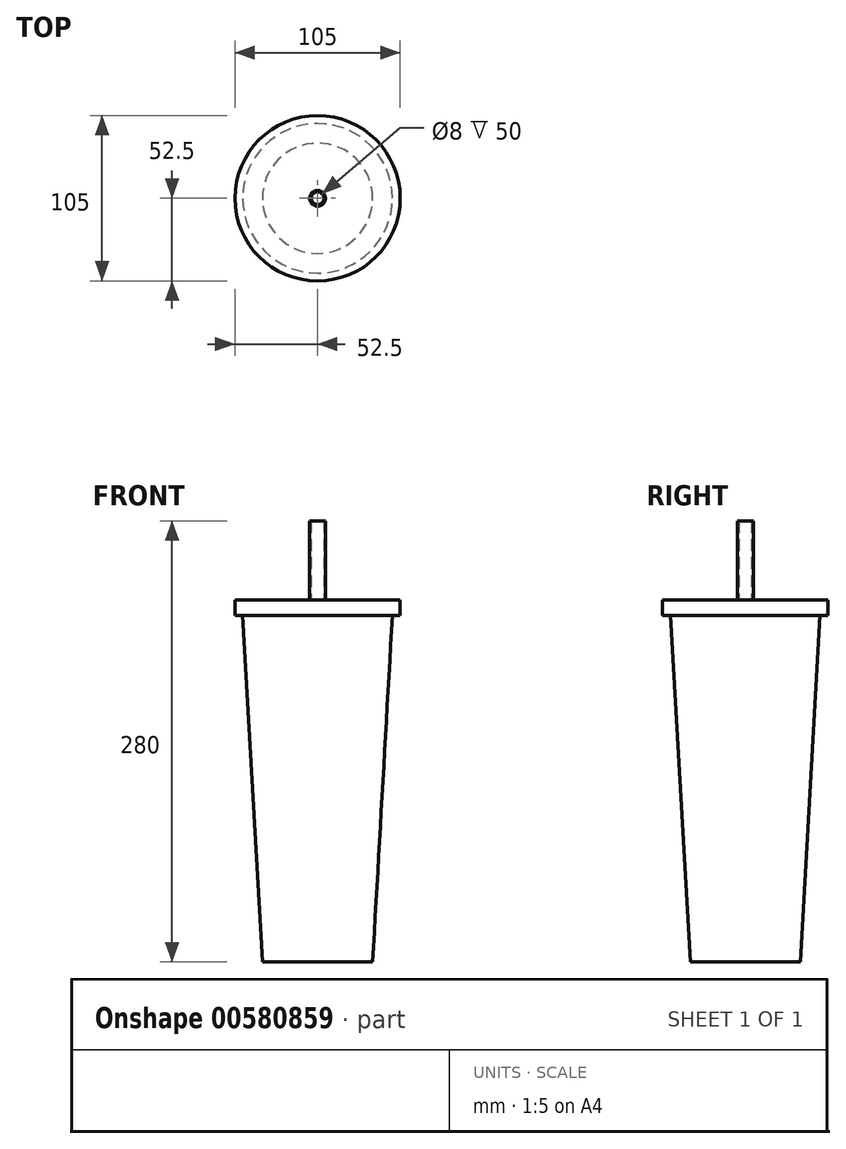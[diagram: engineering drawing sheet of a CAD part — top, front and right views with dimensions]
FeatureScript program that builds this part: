
annotation { "Feature Type Name" : "Feature", "Feature Type Description" : "" }
export const myFeature = defineFeature(function(context is Context, id is Id, definition is map)
    precondition{}
    {
        {
            var Q0;
            Q0=qCreatedBy(makeId("Top.planeOp"),FACE);
            var sketch = newSketch(context, id + "F0", { "sketchPlane" : qUnion([Q0])});
            skCircle(sketch, "E0", {"center": v(0, 0) * mm, "radius": 47.5 * mm});
            skSolve(sketch);
        }
        {
            var Q0;
            Q0=qCreatedBy(makeId("Top.planeOp"),FACE);
            cPlane(context, id + "F1", {"entities" : qUnion([Q0]), "cplaneType" : CPlaneType.OFFSET, "offset" : 220 * mm, "oppositeDirection" : true, "width" : 150 * mm, "height" : 150 * mm});
        }
        {
            var Q0;
            Q0=qCreatedBy(id+"F1.planeOp",FACE);
            var sketch = newSketch(context, id + "F2", { "sketchPlane" : qUnion([Q0])});
            skCircle(sketch, "E1", {"center": v(0, 0) * mm, "radius": 35 * mm});
            skSolve(sketch);
        }
        {
            var Q0;
            Q0=makeQuery(id+"F0.imprint","IMPRINT",FACE,{"disambiguationData":[TD([[makeQuery(id+"F0.imprint","IMPRINT",EDGE,{"derivedFrom":sQuery(id+"F0.wireOp",EDGE,"E0")}),1.0]])]});
            var Q1;
            Q1=makeQuery(id+"F2.imprint","IMPRINT",FACE,{"disambiguationData":[TD([[makeQuery(id+"F2.imprint","IMPRINT",EDGE,{"derivedFrom":sQuery(id+"F2.wireOp",EDGE,"E1")}),1.0]])]});
            loft(context, id + "F3", {"sheetProfilesArray" : [{ "sheetProfileEntities" : qUnion([Q0]) }, { "sheetProfileEntities" : qUnion([Q1]) }]});
        }
        {
            var Q0;
            Q0=makeQuery(id+"F3.opLoft","CAP_FACE",FACE,{"disambiguationData":[OSD([makeQuery(id+"F0.imprint","IMPRINT",FACE,{"disambiguationData":[TD([[makeQuery(id+"F0.imprint","IMPRINT",EDGE,{"derivedFrom":sQuery(id+"F0.wireOp",EDGE,"E0")}),1.0]])]})])],"isStart":true});
            var sketch = newSketch(context, id + "F4", { "sketchPlane" : qUnion([Q0])});
            skCircle(sketch, "E2", {"center": v(0, 0) * mm, "radius": 52.5 * mm});
            skSolve(sketch);
        }
        {
            var Q0;
            Q0=makeQuery(id+"F4.imprint","IMPRINT",FACE,{"disambiguationData":[TD([[makeQuery(id+"F4.imprint","IMPRINT",EDGE,{"derivedFrom":makeQuery(id+"F3.opLoft","MID_CAP_EDGE",EDGE,{"disambiguationData":[OSD([sQuery(id+"F0.wireOp",EDGE,"E0")])],"capPos":0.0})}),-1.0]])]});
            var Q1;
            Q1=makeQuery(id+"F4.imprint","IMPRINT",FACE,{"disambiguationData":[TD([[makeQuery(id+"F4.imprint","IMPRINT",EDGE,{"derivedFrom":sQuery(id+"F4.wireOp",EDGE,"E2")}),1.0]])]});
            extrude(context, id + "F5", {"entities" : qUnion([Q0, Q1]), "operationType" : NewBodyOperationType.ADD, "depth" : 10 * mm, "offsetDistance" : 25 * mm});
        }
        {
            var Q0;
            Q0=makeQuery(id+"F5.opExtrude","CAP_FACE",FACE,{"disambiguationData":[OSD([sQuery(id+"F4.wireOp",EDGE,"E2")])],"isStart":false});
            var sketch = newSketch(context, id + "F6", { "sketchPlane" : qUnion([Q0])});
            skCircle(sketch, "E3", {"center": v(0, 0) * mm, "radius": 5 * mm});
            skCircle(sketch, "E4", {"center": v(0, 0) * mm, "radius": 4 * mm});
            skSolve(sketch);
        }
        {
            var Q0;
            Q0=makeQuery(id+"F6.imprint","IMPRINT",FACE,{"disambiguationData":[TD([[makeQuery(id+"F6.imprint","IMPRINT",EDGE,{"derivedFrom":sQuery(id+"F6.wireOp",EDGE,"E3")}),1.0]])]});
            extrude(context, id + "F7", {"entities" : qUnion([Q0]), "operationType" : NewBodyOperationType.ADD, "depth" : 50 * mm, "offsetDistance" : 25 * mm});
        }
    });
